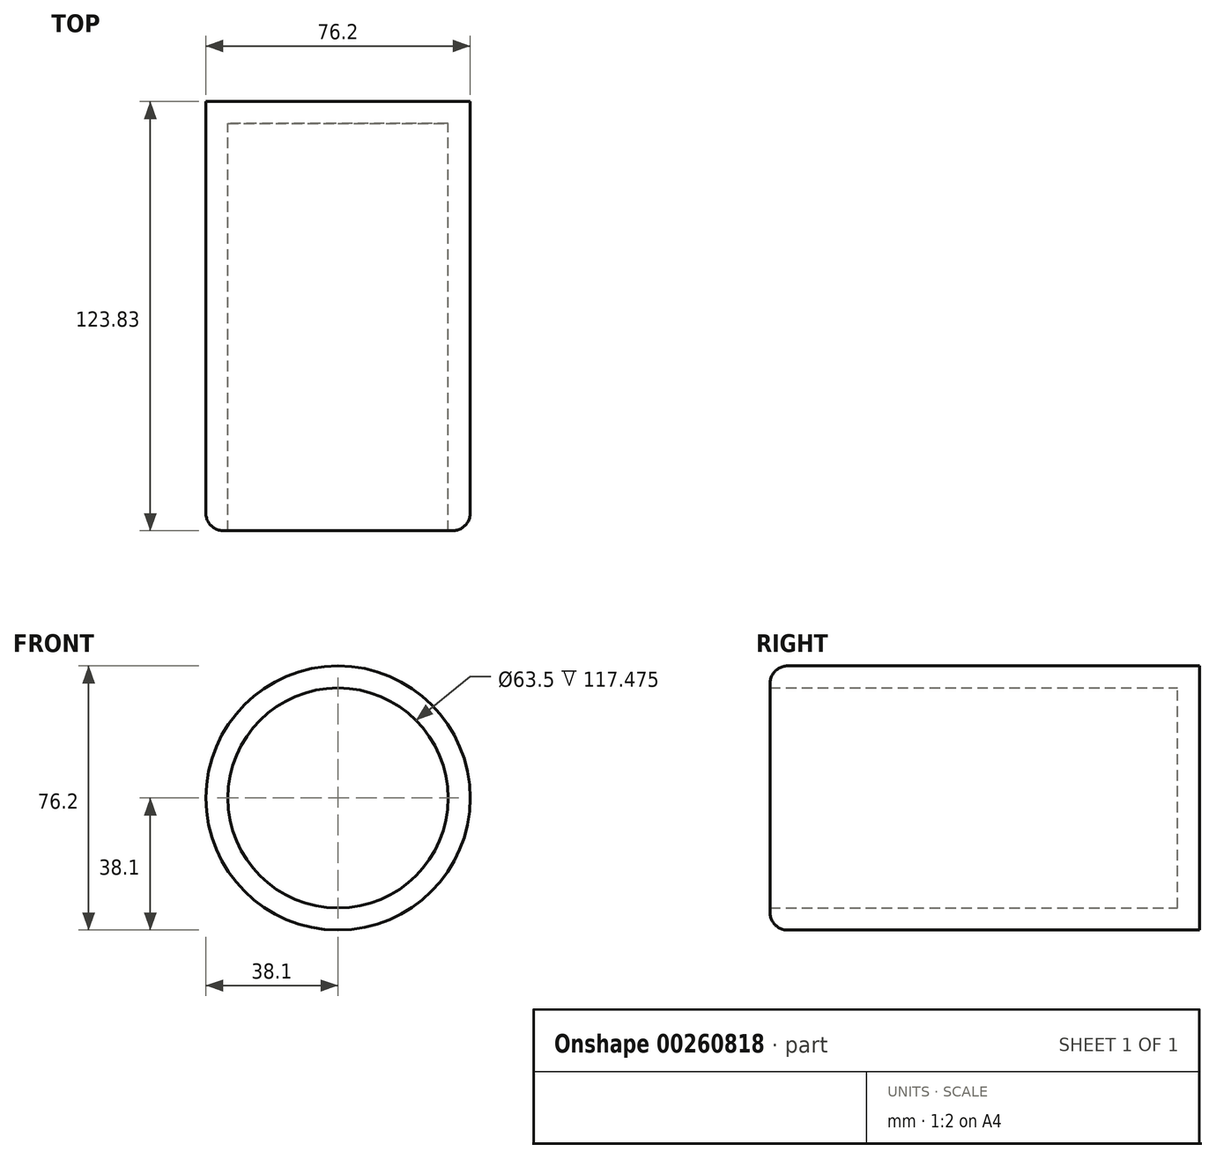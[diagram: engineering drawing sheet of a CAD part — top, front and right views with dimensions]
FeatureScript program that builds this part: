
annotation { "Feature Type Name" : "Feature", "Feature Type Description" : "" }
export const myFeature = defineFeature(function(context is Context, id is Id, definition is map)
    precondition{}
    {
        {
            var Q0;
            Q0=qCreatedBy(makeId("Front.planeOp"),FACE);
            var sketch = newSketch(context, id + "F0", { "sketchPlane" : qUnion([Q0])});
            skCircle(sketch, "E0", {"center": v(0, 0) * mm, "radius": 38.1 * mm});
            skCircle(sketch, "E1", {"center": v(0, 0) * mm, "radius": 31.75 * mm});
            skSolve(sketch);
        }
        {
            var Q0;
            Q0=makeQuery(id+"F0.imprint","IMPRINT",FACE,{"disambiguationData":[TD([[makeQuery(id+"F0.imprint","IMPRINT",EDGE,{"derivedFrom":sQuery(id+"F0.wireOp",EDGE,"E0")}),1.0]])]});
            extrude(context, id + "F1", {"entities" : qUnion([Q0]), "depth" : 123.82 * mm});
        }
        {
            var Q0;
            Q0=qCreatedBy(makeId("Front.planeOp"),FACE);
            var sketch = newSketch(context, id + "F2", { "sketchPlane" : qUnion([Q0])});
            skCircle(sketch, "E2", {"center": v(0, 0) * mm, "radius": 38.1 * mm});
            skSolve(sketch);
        }
        {
            var Q0;
            Q0 = qSketchRegion(id + "F2", true);
            extrude(context, id + "F3", {"entities" : qUnion([Q0]), "operationType" : NewBodyOperationType.ADD, "depth" : 6.35 * mm});
        }
        {
            var Q0;
            Q0=makeQuery(id+"F1.opExtrude","CAP_EDGE",EDGE,{"disambiguationData":[OSD([sQuery(id+"F0.wireOp",EDGE,"E0")])],"isStart":false});
            fillet(context, id + "F4", {"entities" : qUnion([Q0]), "radius" : 5.08 * mm, "tangentPropagation" : true, "allowEdgeOverflow" : false});
        }
    });
